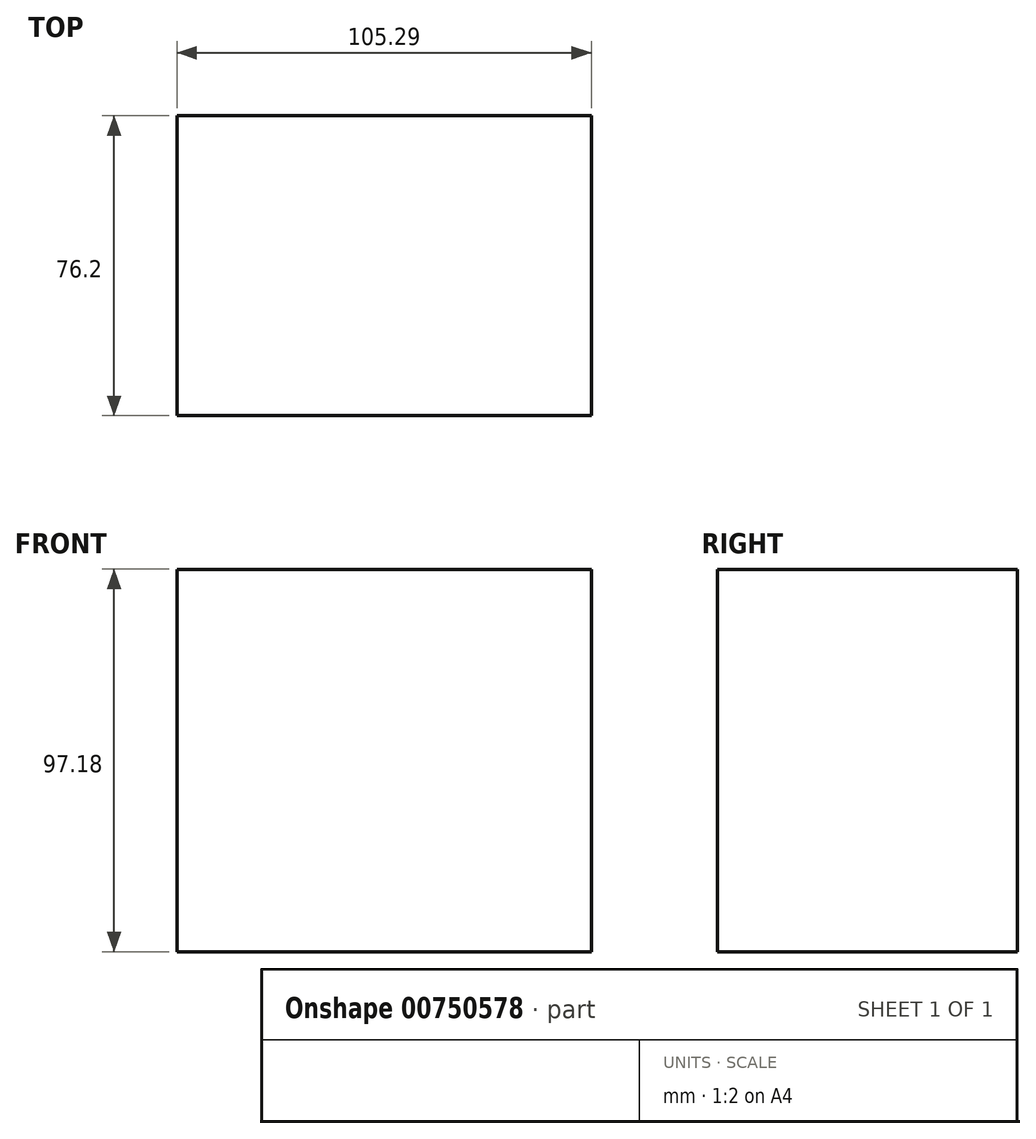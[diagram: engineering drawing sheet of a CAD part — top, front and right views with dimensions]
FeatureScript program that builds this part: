
annotation { "Feature Type Name" : "Feature", "Feature Type Description" : "" }
export const myFeature = defineFeature(function(context is Context, id is Id, definition is map)
    precondition{}
    {
        {
            var Q0;
            Q0=qCreatedBy(makeId("Front.planeOp"),FACE);
            var sketch = newSketch(context, id + "F0", { "sketchPlane" : qUnion([Q0])});
            skLineSegment(sketch, "E0.bottom", {"start": v(-54.58, 53.79) * mm, "end": v(50.71, 53.79) * mm});
            skLineSegment(sketch, "E0.top", {"start": v(-54.58, -43.4) * mm, "end": v(50.71, -43.4) * mm});
            skLineSegment(sketch, "E0.left", {"start": v(-54.58, 53.79) * mm, "end": v(-54.58, -43.4) * mm});
            skLineSegment(sketch, "E0.right", {"start": v(50.71, 53.79) * mm, "end": v(50.71, -43.4) * mm});
            skSolve(sketch);
        }
        {
            var Q0;
            Q0=makeQuery(id+"F0.imprint","IMPRINT",FACE,{"disambiguationData":[TD([[makeQuery(id+"F0.imprint","IMPRINT",EDGE,{"derivedFrom":sQuery(id+"F0.wireOp",EDGE,"E0.bottom")}),-1.0]])]});
            extrude(context, id + "F1", {"entities" : qUnion([Q0]), "oppositeDirection" : true, "depth" : 76.2 * mm, "offsetDistance" : 25.4 * mm});
        }
    });
